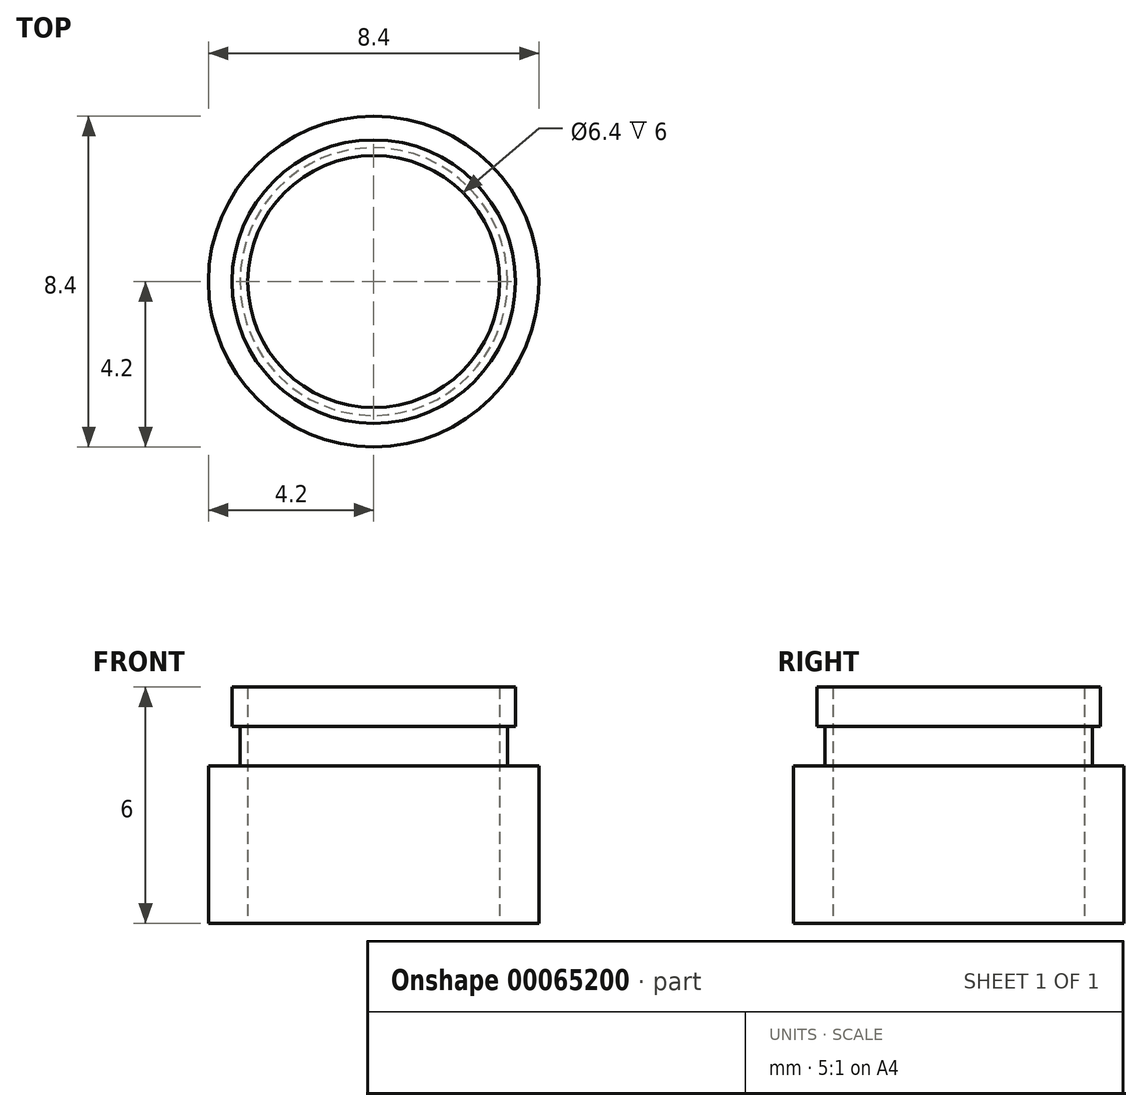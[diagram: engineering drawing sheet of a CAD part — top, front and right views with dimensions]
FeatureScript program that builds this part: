
annotation { "Feature Type Name" : "Feature", "Feature Type Description" : "" }
export const myFeature = defineFeature(function(context is Context, id is Id, definition is map)
    precondition{}
    {
        {
            var Q0;
            Q0=qCreatedBy(makeId("Front.planeOp"),FACE);
            var sketch = newSketch(context, id + "F0", { "sketchPlane" : qUnion([Q0])});
            skLineSegment(sketch, "E0", {"start": v(0, 0) * mm, "end": v(0, 17.68) * mm, "construction": true});
            skLineSegment(sketch, "E1", {"start": v(0, 0) * mm, "end": v(4.2, 0) * mm, "construction": true});
            skLineSegment(sketch, "E2", {"start": v(4.2, 0) * mm, "end": v(4.2, 4) * mm});
            skLineSegment(sketch, "E3", {"start": v(4.2, 4) * mm, "end": v(3.4, 4) * mm});
            skLineSegment(sketch, "E4", {"start": v(3.4, 4) * mm, "end": v(3.4, 5) * mm});
            skLineSegment(sketch, "E5", {"start": v(3.4, 5) * mm, "end": v(3.6, 5) * mm});
            skLineSegment(sketch, "E6", {"start": v(3.6, 5) * mm, "end": v(3.6, 6) * mm});
            skLineSegment(sketch, "E7", {"start": v(3.6, 6) * mm, "end": v(3.4, 6) * mm});
            skLineSegment(sketch, "E8", {"start": v(3.4, 6) * mm, "end": v(3.2, 6) * mm});
            skLineSegment(sketch, "E9", {"start": v(3.2, 6) * mm, "end": v(3.2, 0) * mm});
            skLineSegment(sketch, "E10", {"start": v(3.2, 0) * mm, "end": v(4.2, 0) * mm});
            skSolve(sketch);
        }
        {
            var Q0;
            Q0=makeQuery(id+"F0.imprint","IMPRINT",FACE,{"disambiguationData":[TD([[makeQuery(id+"F0.imprint","IMPRINT",EDGE,{"derivedFrom":sQuery(id+"F0.wireOp",EDGE,"E2")}),1.0]])]});
            var Q1;
            Q1=sQuery(id+"F0.wireOp",EDGE,"E0");
            revolve(context, id + "F1", {"entities" : qUnion([Q0]), "axis" : qUnion([Q1]), "revolveType" : RevolveType.FULL});
        }
    });
